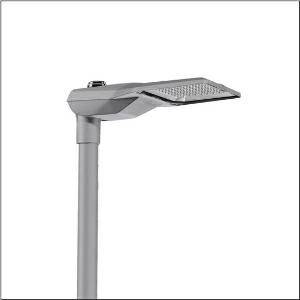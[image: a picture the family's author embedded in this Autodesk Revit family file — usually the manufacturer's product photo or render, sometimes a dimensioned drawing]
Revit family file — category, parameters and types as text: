
# Revit family: streetlight_sl_21_midi___pl52_5xe7h47n08lb_ccfd
name_source: partatom
category: Lighting Fixtures
units: mm (PartAtom-declared; Revit-internal decimal feet)

## family parameters
Cut with Voids When Loaded = No
Host = Face
Light Source = No
Part Type = Normal
Room Calculation Point = No
Round Connector Dimension = Use Diameter
Shared = No

## types (1)
- --- (1 x LED, 14690 lm, 98.3 W, 4000K)
    Apparent Load = 98 VA
    CIE Flux Codes = 27 59 98 100 100
    Color Rendering = 70
    Color Temperature = 4000K
    Default Elevation = 1800 mm
    Description = Streetlight SL 21 midi, mast luminaire, primary light control with lens, of PMMA, primary optical cover: cover, of toughened safety glass, transparent, light distribution: PL52, light emission: direct distribution, primary light characteristic: asymmetric, installation type: side-entry, LED, 3G 2.5mm², High Power LED, rated luminous flux: 14.690lm, luminous efficacy: 149lm/W, light colour: 740, colour temperature: 4000K, control: overheat protection, presetting dimming linear, constant luminous flux control, time-dependent luminous flux control, flexible luminous flux parameterisation, mains connection: 220..240V, AC, 50/60Hz, connection cable pre-assembled, cable length: 10,5m, wiring characteristics: H05VV-F, start of lifetime: 98W, end of service life: 101W, reduction: 45W, luminaire housing, of diecast aluminium (EN AC-44300), powder-coated, Siteco® metallic grey (DB 702S), corrosivity category C5 mid according to DIN EN ISO 12944, multi-level sealing system, sealing non-destructively replaceable, inclination adjustable: 0°, 5°, 10°, 15°, length: 644mm, width: 335mm, height: 110mm, spigot size: 42mm (side-entry), protection rating (complete): IP66, insulation class (complete): insulation class I (protective earthing), certification: CE, ENEC, ENEC+, VDE, impact resistance: IK09, permissible operating ambient temperature for outdoor applications: -40..+50°C, standard-compliant lighting for roads and squares, packaging unit: 1 piece

Light Distribution: PL52
    Height = 111 mm
    Lamp = 1 x LED
    Lamp Light Flux = 14690 lm
    Lamp Power = 98.3 W
    Lamp count = 1
    Length = 644 mm
    Luminous efficacy = 149 lm/W
    Manufacturer = Siteco
    ModVariant = No
    Model = 5XE7H47N08LB
    Number of Poles = 1
    OnlyDefault = Yes
    Power Factor = 1
    Product Name = Streetlight SL 21 midi | PL52
    Product group = mast luminaire | pylon top
    ProductGroupID = 6100
    Protection Class = Protection class I
    Protection Degree = IP 66
    RLX_Detail_Level = 1
    RLX_Emergency_Light_Flux = 0 lm
    RLX_Emergency_Type = 0
    RLX_Emergency_Type_DB = No
    RlxData = <blob elided: 100265 chars, md5=2effa972>
    Socket = socket
    Standby Power = 0 W
    System Light Flux = 14690 lm
    System Power = 98 W
    Type Comments = factory setting: luminous flux: 100 % | dim-lin: 254 | 1020 mA
    Type Image = l_1294377.jpg
    URL = http://relux.com
    VarID = @adj_086225
    Voltage = 0 V
    Weight = 0.00 kg
    Width = 336 mm

## geometry (parser evidence)
native form markers: Blend x4, Sweep x10
no freeform markers — native parametric forms only
